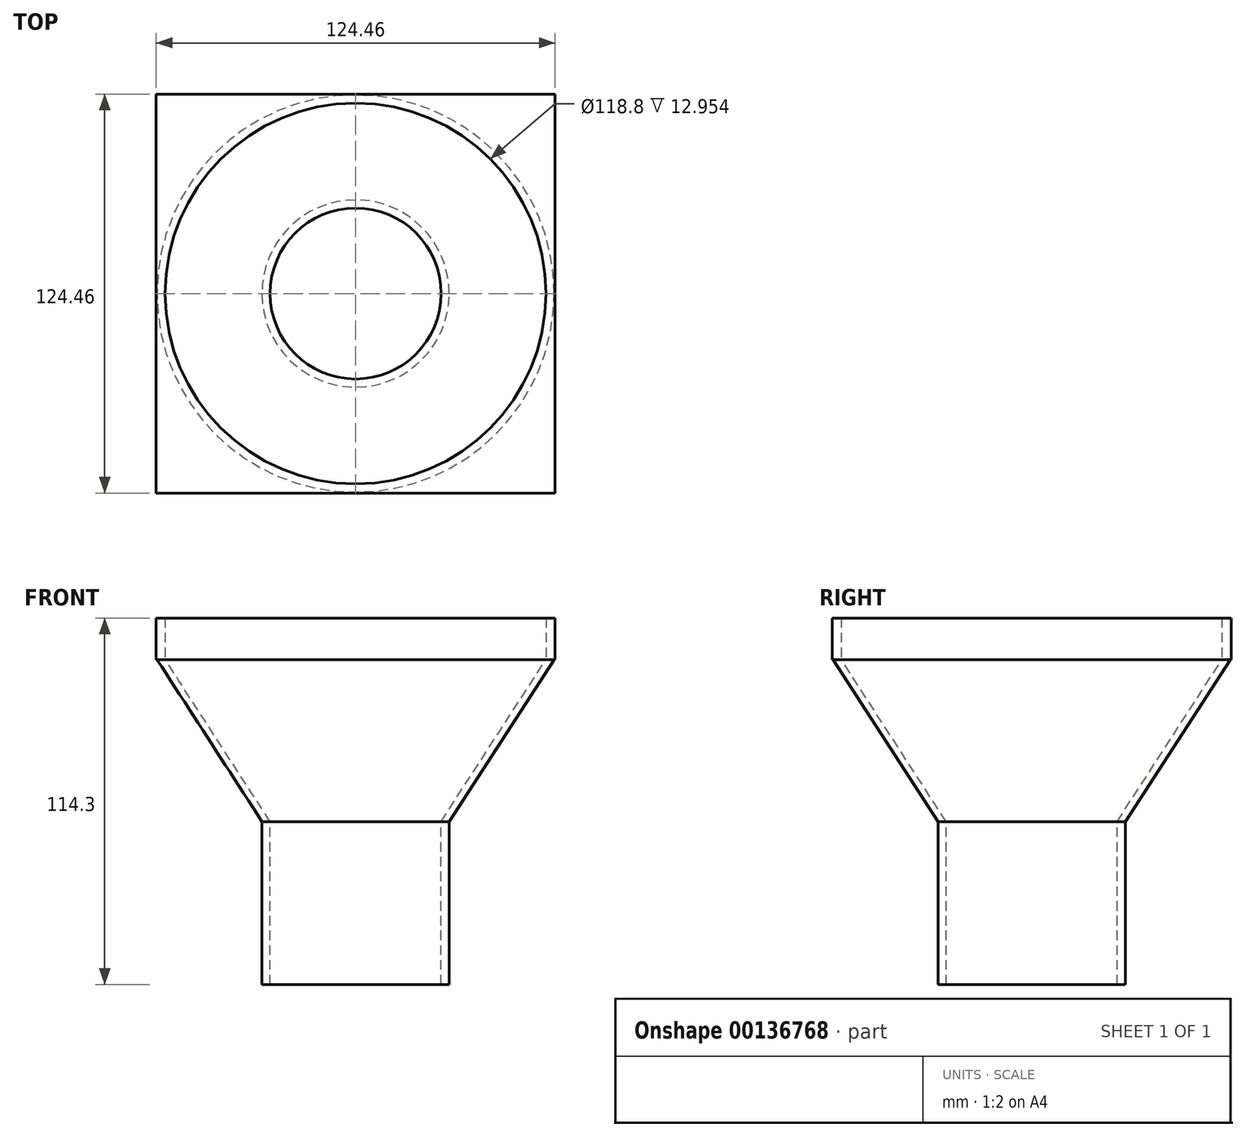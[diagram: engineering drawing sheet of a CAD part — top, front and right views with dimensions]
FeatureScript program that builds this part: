
annotation { "Feature Type Name" : "Feature", "Feature Type Description" : "" }
export const myFeature = defineFeature(function(context is Context, id is Id, definition is map)
    precondition{}
    {
        {
            var Q0;
            Q0=qCreatedBy(makeId("Top.planeOp"),FACE);
            var sketch = newSketch(context, id + "F0", { "sketchPlane" : qUnion([Q0])});
            skLineSegment(sketch, "E0", {"start": v(0, 0) * mm, "end": v(0, 62.23) * mm});
            skLineSegment(sketch, "E1", {"start": v(0, 0) * mm, "end": v(0, -62.23) * mm});
            skLineSegment(sketch, "E2", {"start": v(0, 0) * mm, "end": v(-62.23, 0) * mm});
            skLineSegment(sketch, "E3", {"start": v(0, 0) * mm, "end": v(62.23, 0) * mm});
            skLineSegment(sketch, "E4", {"start": v(0, 62.23) * mm, "end": v(-62.23, 62.23) * mm});
            skLineSegment(sketch, "E5", {"start": v(-62.23, 62.23) * mm, "end": v(-62.23, -62.23) * mm});
            skLineSegment(sketch, "E6", {"start": v(-62.23, -62.23) * mm, "end": v(62.23, -62.23) * mm});
            skLineSegment(sketch, "E7", {"start": v(62.23, -62.23) * mm, "end": v(62.23, 62.23) * mm});
            skLineSegment(sketch, "E8", {"start": v(0, 62.23) * mm, "end": v(62.23, 62.23) * mm});
            skSolve(sketch);
        }
        {
            var Q0;
            Q0 = qSketchRegion(id + "F0", true);
            extrude(context, id + "F1", {"entities" : qUnion([Q0]), "oppositeDirection" : true, "depth" : 12.7 * mm});
        }
        {
            var Q0;
            Q0=makeQuery(id+"F1.opExtrude","CAP_FACE",FACE,{"disambiguationData":[OSD([sQuery(id+"F0.wireOp",EDGE,"E4"),sQuery(id+"F0.wireOp",EDGE,"E5"),sQuery(id+"F0.wireOp",EDGE,"E6"),sQuery(id+"F0.wireOp",EDGE,"E7"),sQuery(id+"F0.wireOp",EDGE,"E8")])],"isStart":false});
            var sketch = newSketch(context, id + "F2", { "sketchPlane" : qUnion([Q0])});
            skSolve(sketch);
        }
        {
            var Q0;
            Q0=makeQuery(id+"F2.imprint","IMPRINT",FACE,{"disambiguationData":[TD([[makeQuery(id+"F2.imprint","IMPRINT",EDGE,{"derivedFrom":makeQuery(id+"F1.opExtrude","CAP_EDGE",EDGE,{"disambiguationData":[OSD([sQuery(id+"F0.wireOp",EDGE,"E5")])],"isStart":false})}),-1.0]])]});
            var sketch = newSketch(context, id + "F3", { "sketchPlane" : qUnion([Q0])});
            skCircle(sketch, "E9", {"center": v(0, 0) * mm, "radius": 62.1 * mm});
            skSolve(sketch);
        }
        {
            var Q0;
            Q0=makeQuery(id+"F2.imprint","IMPRINT",FACE,{"disambiguationData":[TD([[makeQuery(id+"F2.imprint","IMPRINT",EDGE,{"derivedFrom":makeQuery(id+"F1.opExtrude","CAP_EDGE",EDGE,{"disambiguationData":[OSD([sQuery(id+"F0.wireOp",EDGE,"E5")])],"isStart":false})}),-1.0]])]});
            cPlane(context, id + "F4", {"entities" : qUnion([Q0]), "cplaneType" : CPlaneType.OFFSET, "offset" : 50.8 * mm, "width" : 152.4 * mm, "height" : 152.4 * mm});
        }
        {
            var Q0;
            Q0=qCreatedBy(id+"F4.planeOp",FACE);
            var sketch = newSketch(context, id + "F5", { "sketchPlane" : qUnion([Q0])});
            skCircle(sketch, "E10", {"center": v(0, 0) * mm, "radius": 29.21 * mm});
            skSolve(sketch);
        }
        {
            var Q1;
            Q1=makeQuery(id+"F3.imprint","IMPRINT",FACE,{"disambiguationData":[TD([[makeQuery(id+"F3.imprint","IMPRINT",EDGE,{"derivedFrom":sQuery(id+"F3.wireOp",EDGE,"E9")}),1.0]])]});
            var Q2;
            Q2=makeQuery(id+"F5.imprint","IMPRINT",FACE,{"disambiguationData":[TD([[makeQuery(id+"F5.imprint","IMPRINT",EDGE,{"derivedFrom":sQuery(id+"F5.wireOp",EDGE,"E10")}),1.0]])]});
            loft(context, id + "F6", {"operationType" : NewBodyOperationType.ADD, "sheetProfilesArray" : [{ "sheetProfileEntities" : qUnion([Q1]) }, { "sheetProfileEntities" : qUnion([Q2]) }]});
        }
        {
            var Q0;
            Q0=makeQuery(id+"F6.opLoft","CAP_FACE",FACE,{"disambiguationData":[OSD([makeQuery(id+"F5.imprint","IMPRINT",FACE,{"disambiguationData":[TD([[makeQuery(id+"F5.imprint","IMPRINT",EDGE,{"derivedFrom":sQuery(id+"F5.wireOp",EDGE,"E10")}),1.0]])]})])],"isStart":true});
            var sketch = newSketch(context, id + "F7", { "sketchPlane" : qUnion([Q0])});
            skCircle(sketch, "E11", {"center": v(0, 0) * mm, "radius": 26.67 * mm});
            skSolve(sketch);
        }
        {
            var Q0;
            Q0=makeQuery(id+"F1.opExtrude","CAP_FACE",FACE,{"disambiguationData":[OSD([sQuery(id+"F0.wireOp",EDGE,"E4"),sQuery(id+"F0.wireOp",EDGE,"E5"),sQuery(id+"F0.wireOp",EDGE,"E6"),sQuery(id+"F0.wireOp",EDGE,"E7"),sQuery(id+"F0.wireOp",EDGE,"E8")])],"isStart":false});
            var sketch = newSketch(context, id + "F8", { "sketchPlane" : qUnion([Q0])});
            skCircle(sketch, "E12", {"center": v(0, 0) * mm, "radius": 59.56 * mm});
            skSolve(sketch);
        }
        {
            var Q1;
            Q1 = qSketchRegion(id + "F8", true);
            var Q2;
            Q2=makeQuery(id+"F7.imprint","IMPRINT",FACE,{"disambiguationData":[TD([[makeQuery(id+"F7.imprint","IMPRINT",EDGE,{"derivedFrom":sQuery(id+"F7.wireOp",EDGE,"E11")}),1.0]])]});
            loft(context, id + "F9", {"operationType" : NewBodyOperationType.REMOVE, "sheetProfilesArray" : [{ "sheetProfileEntities" : qUnion([Q1]) }, { "sheetProfileEntities" : qUnion([Q2]) }]});
        }
        {
            var Q0;
            Q0 = qSketchRegion(id + "F3", true);
            extrude(context, id + "F10", {"entities" : qUnion([Q0]), "operationType" : NewBodyOperationType.REMOVE, "oppositeDirection" : true, "depth" : 25.4 * mm});
        }
        {
            var Q0;
            Q0=makeQuery(id+"F6.opLoft","CAP_FACE",FACE,{"disambiguationData":[OSD([makeQuery(id+"F5.imprint","IMPRINT",FACE,{"disambiguationData":[TD([[makeQuery(id+"F5.imprint","IMPRINT",EDGE,{"derivedFrom":sQuery(id+"F5.wireOp",EDGE,"E10")}),1.0]])]})])],"isStart":true});
            extrude(context, id + "F11", {"entities" : qUnion([Q0]), "operationType" : NewBodyOperationType.ADD, "depth" : 50.8 * mm});
        }
        {
            var Q0;
            Q0=makeQuery(id+"F2.imprint","IMPRINT",FACE,{"disambiguationData":[TD([[makeQuery(id+"F2.imprint","IMPRINT",EDGE,{"derivedFrom":makeQuery(id+"F1.opExtrude","CAP_EDGE",EDGE,{"disambiguationData":[OSD([sQuery(id+"F0.wireOp",EDGE,"E5")])],"isStart":false})}),-1.0]])]});
            extrude(context, id + "F12", {"entities" : qUnion([Q0]), "operationType" : NewBodyOperationType.ADD, "depth" : 0.25 * mm});
        }
        {
            var Q0;
            Q0=makeQuery(id+"F12.boolean.opBoolean","SPLIT",FACE,{"disambiguationData":[TD([makeQuery(id+"F9.boolean.opBoolean","COPY",FACE,{"derivedFrom":makeQuery(id+"F9.opLoft","SWEPT_FACE",FACE,{"disambiguationData":[OSD([sQuery(id+"F3.wireOp",EDGE,"E9"),sQuery(id+"F7.wireOp",EDGE,"E11")])]})})])],"derivedFrom":makeQuery(id+"F12.opExtrude","CAP_FACE",FACE,{"disambiguationData":[OSD([sQuery(id+"F0.wireOp",EDGE,"E4"),sQuery(id+"F0.wireOp",EDGE,"E5"),sQuery(id+"F0.wireOp",EDGE,"E6"),sQuery(id+"F0.wireOp",EDGE,"E7"),sQuery(id+"F0.wireOp",EDGE,"E8")])],"isStart":false})});
            extrude(context, id + "F13", {"entities" : qUnion([Q0]), "operationType" : NewBodyOperationType.REMOVE, "oppositeDirection" : true, "depth" : 25.4 * mm});
        }
        {
            var Q0;
            Q0=makeQuery(id+"F1.opExtrude","CAP_FACE",FACE,{"disambiguationData":[OSD([sQuery(id+"F0.wireOp",EDGE,"E4"),sQuery(id+"F0.wireOp",EDGE,"E5"),sQuery(id+"F0.wireOp",EDGE,"E6"),sQuery(id+"F0.wireOp",EDGE,"E7"),sQuery(id+"F0.wireOp",EDGE,"E8")])],"isStart":true});
            var sketch = newSketch(context, id + "F14", { "sketchPlane" : qUnion([Q0])});
            skLineSegment(sketch, "E13.bottom", {"start": v(-62.23, 62.23) * mm, "end": v(62.23, 62.23) * mm});
            skLineSegment(sketch, "E13.top", {"start": v(-62.23, -62.23) * mm, "end": v(62.23, -62.23) * mm});
            skLineSegment(sketch, "E13.left", {"start": v(-62.23, 62.23) * mm, "end": v(-62.23, -62.23) * mm});
            skLineSegment(sketch, "E13.right", {"start": v(62.23, 62.23) * mm, "end": v(62.23, -62.23) * mm});
            skSolve(sketch);
        }
        {
            var Q0;
            Q0 = qSketchRegion(id + "F14", true);
            extrude(context, id + "F15", {"entities" : qUnion([Q0]), "operationType" : NewBodyOperationType.ADD, "oppositeDirection" : true, "depth" : 2.54 * mm});
        }
        {
            var Q0;
            {var subQ0=sQuery(id+"FWlMah1EWGIa96Z_1.wireOp",EDGE,"rE7WOWhX-8PW8-ZHOG-MU93-Pz0rNFo2tsMe.right");var subQ1=sQuery(id+"FWlMah1EWGIa96Z_1.wireOp",EDGE,"rE7WOWhX-8PW8-ZHOG-MU93-Pz0rNFo2tsMe.left");var subQ2=sQuery(id+"FWlMah1EWGIa96Z_1.wireOp",EDGE,"rE7WOWhX-8PW8-ZHOG-MU93-Pz0rNFo2tsMe.top");var subQ3=sQuery(id+"FWlMah1EWGIa96Z_1.wireOp",EDGE,"rE7WOWhX-8PW8-ZHOG-MU93-Pz0rNFo2tsMe.bottom");var subQ4=sQuery(id+"F7.wireOp",EDGE,"E11");var subQ5=sQuery(id+"F3.wireOp",EDGE,"E9");Q0=makeQuery(id+"F15.boolean.opBoolean","SPLIT",FACE,{"disambiguationData":[TD([makeQuery(id+"FkfeMjda3U2Uokb_1.boolean.opBoolean","COPY",FACE,{"derivedFrom":makeQuery(id+"FkfeMjda3U2Uokb_1.opExtrude","SWEPT_FACE",FACE,{"disambiguationData":[OSD([subQ5,subQ4,subQ3,subQ2,subQ1,subQ0])]})})])],"derivedFrom":makeQuery(id+"F15.opExtrude","CAP_FACE",FACE,{"disambiguationData":[OSD([sQuery(id+"F14.wireOp",EDGE,"E13.bottom"),sQuery(id+"F14.wireOp",EDGE,"E13.top"),sQuery(id+"F14.wireOp",EDGE,"E13.left"),sQuery(id+"F14.wireOp",EDGE,"E13.right")])],"isStart":false})});}
            extrude(context, id + "F16", {"entities" : qUnion([Q0]), "operationType" : NewBodyOperationType.REMOVE, "oppositeDirection" : true, "depth" : 25.4 * mm});
        }
        {
            var Q0;
            Q0=makeQuery(id+"F12.boolean.opBoolean","MERGE",FACE,{"derivedFrom":[makeQuery(id+"F10.boolean.opBoolean","COPY",FACE,{"derivedFrom":makeQuery(id+"F10.opExtrude","CAP_FACE",FACE,{"disambiguationData":[OSD([sQuery(id+"F3.wireOp",EDGE,"E9")])],"isStart":true})}),makeQuery(id+"F12.opExtrude","CAP_FACE",FACE,{"disambiguationData":[OSD([sQuery(id+"F0.wireOp",EDGE,"E4"),sQuery(id+"F0.wireOp",EDGE,"E5"),sQuery(id+"F0.wireOp",EDGE,"E6"),sQuery(id+"F0.wireOp",EDGE,"E7"),sQuery(id+"F0.wireOp",EDGE,"E8")])],"isStart":true})]});
            extrude(context, id + "F17", {"entities" : qUnion([Q0]), "operationType" : NewBodyOperationType.ADD, "depth" : 12.7 * mm});
        }
    });
